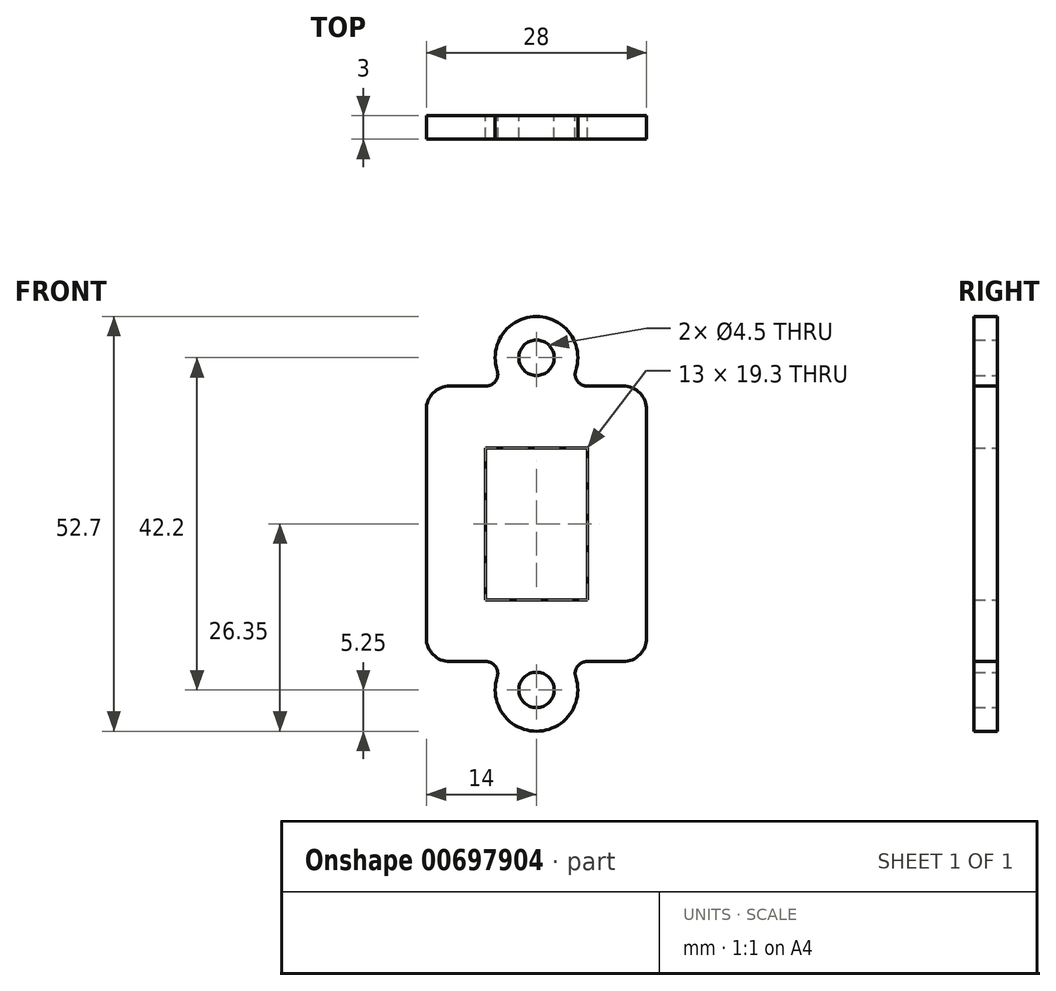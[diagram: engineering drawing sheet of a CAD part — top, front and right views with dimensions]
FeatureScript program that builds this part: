
annotation { "Feature Type Name" : "Feature", "Feature Type Description" : "" }
export const myFeature = defineFeature(function(context is Context, id is Id, definition is map)
    precondition{}
    {
        {
            var Q0;
            Q0=qCreatedBy(makeId("Front.planeOp"),FACE);
            var sketch = newSketch(context, id + "F0", { "sketchPlane" : qUnion([Q0])});
            skLineSegment(sketch, "E0.bottom", {"start": v(-11, 17.5) * mm, "end": v(-6.42, 17.5) * mm});
            skLineSegment(sketch, "E0.top", {"start": v(-11, -17.5) * mm, "end": v(-6.42, -17.5) * mm});
            skLineSegment(sketch, "E0.left", {"start": v(-14, 14.5) * mm, "end": v(-14, -14.5) * mm});
            skLineSegment(sketch, "E0.right", {"start": v(14, 14.5) * mm, "end": v(14, -14.5) * mm});
            skPoint(sketch, "E0.middle", {"position": v(0, 0) * mm});
            skLineSegment(sketch, "E1.bottom", {"start": v(-6.5, 9.65) * mm, "end": v(6.5, 9.65) * mm});
            skLineSegment(sketch, "E1.top", {"start": v(-6.5, -9.65) * mm, "end": v(6.5, -9.65) * mm});
            skLineSegment(sketch, "E1.left", {"start": v(-6.5, 9.65) * mm, "end": v(-6.5, -9.65) * mm});
            skLineSegment(sketch, "E1.right", {"start": v(6.5, 9.65) * mm, "end": v(6.5, -9.65) * mm});
            skCircle(sketch, "E2", {"center": v(0, 21.1) * mm, "radius": 2.25 * mm});
            skArc(sketch, "E3.0", {"start": v(4.99, 19.47) * mm, "mid": v(0, 26.35) * mm, "end": v(-4.99, 19.47) * mm});
            skArc(sketch, "E4", {"start": v(-6.42, 17.5) * mm, "mid": v(-5.2, 18.12) * mm, "end": v(-4.99, 19.47) * mm});
            skArc(sketch, "E5", {"start": v(4.99, 19.47) * mm, "mid": v(5.2, 18.12) * mm, "end": v(6.42, 17.5) * mm});
            skLineSegment(sketch, "E6.trimOffspring", {"start": v(6.42, 17.5) * mm, "end": v(11, 17.5) * mm});
            skArc(sketch, "E7.MirrorCS", {"start": v(-6.42, -17.5) * mm, "mid": v(-5.2, -18.12) * mm, "end": v(-4.99, -19.47) * mm});
            skArc(sketch, "E8.MirrorCS", {"start": v(4.99, -19.47) * mm, "mid": v(0, -26.35) * mm, "end": v(-4.99, -19.47) * mm});
            skArc(sketch, "E9.MirrorCS", {"start": v(4.99, -19.47) * mm, "mid": v(5.2, -18.12) * mm, "end": v(6.42, -17.5) * mm});
            skCircle(sketch, "E10.MirrorC", {"center": v(0, -21.1) * mm, "radius": 2.25 * mm});
            skLineSegment(sketch, "E11.trimOffspring", {"start": v(6.42, -17.5) * mm, "end": v(11, -17.5) * mm});
            skPoint(sketch, "E12.visualSharp", {"position": v(-14, 17.5) * mm});
            skArc(sketch, "E12.filletArc", {"start": v(-11, 17.5) * mm, "mid": v(-13.12, 16.62) * mm, "end": v(-14, 14.5) * mm});
            skPoint(sketch, "E13.visualSharp", {"position": v(-14, -17.5) * mm});
            skArc(sketch, "E13.filletArc", {"start": v(-14, -14.5) * mm, "mid": v(-13.12, -16.62) * mm, "end": v(-11, -17.5) * mm});
            skPoint(sketch, "E14.visualSharp", {"position": v(14, -17.5) * mm});
            skArc(sketch, "E14.filletArc", {"start": v(11, -17.5) * mm, "mid": v(13.12, -16.62) * mm, "end": v(14, -14.5) * mm});
            skPoint(sketch, "E15.visualSharp", {"position": v(14, 17.5) * mm});
            skArc(sketch, "E15.filletArc", {"start": v(14, 14.5) * mm, "mid": v(13.12, 16.62) * mm, "end": v(11, 17.5) * mm});
            skSolve(sketch);
        }
        {
            var Q0;
            Q0 = qSketchRegion(id + "F0", true);
            var Q1;
            Q1=makeQuery(id+"F0.imprint","IMPRINT",FACE,{"disambiguationData":[TD([[makeQuery(id+"F0.imprint","IMPRINT",EDGE,{"derivedFrom":sQuery(id+"F0.wireOp",EDGE,"0300936e-cfb5-4b52-986f-c9d425e3e706.sketch_text.stroke-62")}),1.0]])]});
            var Q2;
            Q2=makeQuery(id+"F0.imprint","IMPRINT",FACE,{"disambiguationData":[TD([[makeQuery(id+"F0.imprint","IMPRINT",EDGE,{"derivedFrom":sQuery(id+"F0.wireOp",EDGE,"0300936e-cfb5-4b52-986f-c9d425e3e706.sketch_text.stroke-23")}),1.0]])]});
            extrude(context, id + "F1", {"entities" : qUnion([Q0, Q1, Q2]), "depth" : 3 * mm, "offsetDistance" : 25 * mm});
        }
    });
